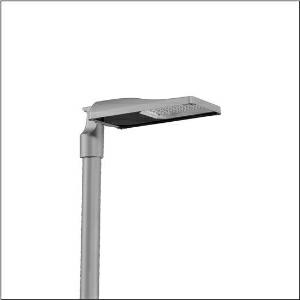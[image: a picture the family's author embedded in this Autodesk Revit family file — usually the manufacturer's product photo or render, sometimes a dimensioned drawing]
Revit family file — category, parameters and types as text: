
# Revit family: streetlight_sl_31_mini___st1_0a_5xh6d3ab08ja_7089
name_source: partatom
category: Lighting Fixtures
units: mm (PartAtom-declared; Revit-internal decimal feet)

## family parameters
Cut with Voids When Loaded = No
Host = Face
Light Source = No
Part Type = Normal
Room Calculation Point = No
Round Connector Dimension = Use Diameter
Shared = No

## types (1)
- --- (1 x LED, 12140 lm, 81.1 W, 3000K)
    Apparent Load = 81 VA
    CIE Flux Codes = 40 73 97 100 100
    Color Rendering = 70
    Color Temperature = 3000K
    Default Elevation = 1800 mm
    Description = Streetlight SL 31 mini Easy LST mast luminaire for post-top, side-entry; light control with lens of PMMA; light distribution: ST1.0a, direct asymmetric distribution, for standard-compliant lighting for roads and squares; LED: luminous flux: 12.140lm, light colour: 730, colour temperature: 3000K; luminous efficacy: 149,7lm/W; control: pre-setting: linear dimming characteristic, flexible luminous flux parameterisation, time-dependent luminous flux control, constant luminous flux control, power reduction, intelligent temperature release in ECG and LED module, overheat protection; luminaire housing, of diecast aluminium, SITECO metallic grey (DB 702S), corrosivity category C5 high according to DIN EN ISO 12944; cover of toughened safety glass, transparent, opened without tools; mast flange of diecast aluminium, SITECO metallic grey (DB 702S), spigot size: 76/60mm, mast flange included unmounted; cable length: 10,5m, connection cable pre-assembled; mains connection: 220..240V, AC, 50/60Hz; power consumption (at start of service life): 81,1W / (at end of service life): 88,3W / (with reduced operation 50%): 36,4W; protection rating (complete): IP66; insulation class (complete): insulation class II (safety insulation); impact resistance: IK10; certification: CE, ENEC, ENEC+, VDE, UKCA; permissible operating ambient temperature for outdoor applications: -40..+50°C; packaging unit: 1 piece

Light Distribution: ST1.0a
    Height = 76 mm
    Lamp = 1 x LED
    Lamp Light Flux = 12140 lm
    Lamp Power = 81.1 W
    Lamp count = 1
    Length = 547 mm
    Luminous efficacy = 150 lm/W
    Manufacturer = Siteco
    ModVariant = No
    Model = 5XH6D3AB08JA
    Number of Poles = 1
    OnlyDefault = Yes
    Power Factor = 1
    Product Name = Streetlight SL 31 mini | ST1.0a
    Product group = mast luminaire | pylon top
    ProductGroupID = 6100
    Protection Class = Protection class II
    Protection Degree = IP 66
    RLX_Detail_Level = 1
    RLX_Emergency_Light_Flux = 0 lm
    RLX_Emergency_Type = 0
    RLX_Emergency_Type_DB = No
    RlxData = <blob elided: 39689 chars, md5=cfdffe91>
    Socket = socket
    Standby Power = 0 W
    System Light Flux = 12140 lm
    System Power = 81 W
    Type Comments = factory setting: luminous flux: 100 % | dim-lin: 254 | 860 mA
    Type Image = l_1300326.jpg
    URL = http://relux.com
    VarID = @adj_057275
    Voltage = 0 V
    Weight = 0.00 kg
    Width = 265 mm

## geometry (parser evidence)
native form markers: Blend x4, Sweep x9
no freeform markers — native parametric forms only
